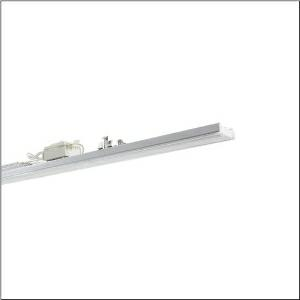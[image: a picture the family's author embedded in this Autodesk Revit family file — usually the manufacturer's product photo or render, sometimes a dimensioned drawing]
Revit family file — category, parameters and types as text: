
# Revit family: licross_r__11_recessed_extreme_mo_51tl12dv4fxge_0dac
name_source: partatom
category: Lighting Fixtures
units: mm (PartAtom-declared; Revit-internal decimal feet)

## family parameters
Cut with Voids When Loaded = No
Host = Face
Light Source = No
Part Type = Normal
Room Calculation Point = No
Round Connector Dimension = Use Diameter
Shared = No

## types (1)
- --- (1 x LED, 15360 lm, 84.1 W, 4000K)
    Apparent Load = 84 VA
    CIE Flux Codes = 67 92 99 100 100
    Color Rendering = 80
    Color Temperature = 4000K
    Default Elevation = 1800 mm
    Description = Licross® 11 Recessed extreme MO, luminaire insert, of sheet steel, coil coated, white, length: 2.250mm, width: 66mm, height: 67mm, LED rated luminous flux: 15.360lm, light colour: 840, control gear: DALI 2, with plug, 5-pole, with phase selection, mains connection: 220..240V, AC, 50/60Hz, rated input power: 84W, halogen-free wiring, primary optical cover: cover, of PMMA, light emission: direct distribution, primary light characteristic: symmetric, protection rating (complete): IP40, insulation class (complete): insulation class I (protective earthing), certification: CE, ENEC, VDE, UKCA, protection symbol: D if used in an environment without relevant dust loads with corresponding accessories, impact resistance: IK06, permissible ambient temperature for indoor applications: -40..+45°C, corresponds to IFS (International Featured Standards) requirements for safety and quality in the food industry, reducing of maximum allowable ambient temperature of 5°C with ceiling mounting, LABS conformity tested according to VDMA 24364:2018-05, packaging unit: 1 piece
    Height = 58 mm
    Lamp = 1 x LED
    Lamp Light Flux = 15360 lm
    Lamp Power = 84.1 W
    Lamp count = 1
    Length = 2250 mm
    Luminous efficacy = 183 lm/W
    Manufacturer = Siteco
    ModVariant = No
    Model = 51TL12DV4FXGE
    Mounting Place = Ceiling
    Mounting Type = Pendant
    Number of Poles = 1
    OnlyDefault = Yes
    Power Factor = 1
    Product Name = Licross® 11 Recessed extreme MO
    Product group = luminaire insert
    ProductGroupID = 902
    Protection Class = Protection class I
    Protection Degree = IP 40
    RLX_Detail_Level = 1
    RLX_Emergency_Light_Flux = 0 lm
    RLX_Emergency_Type = 0
    RLX_Emergency_Type_DB = No
    RlxData = <blob elided: 29457 chars, md5=91015ab0>
    Socket = socket
    Standby Power = 0 W
    System Light Flux = 15360 lm
    System Power = 84 W
    Type Comments = factory setting: luminous flux: 100 % | dim-lin: 254 | 378 mA
    Type Image = l_1296930.jpg
    URL = http://relux.com
    VarID = @adj_082488
    Voltage = 0 V
    Weight = 0.00 kg
    Width = 66 mm

## geometry (parser evidence)
native form markers: Blend x4, Sweep x10
no freeform markers — native parametric forms only
